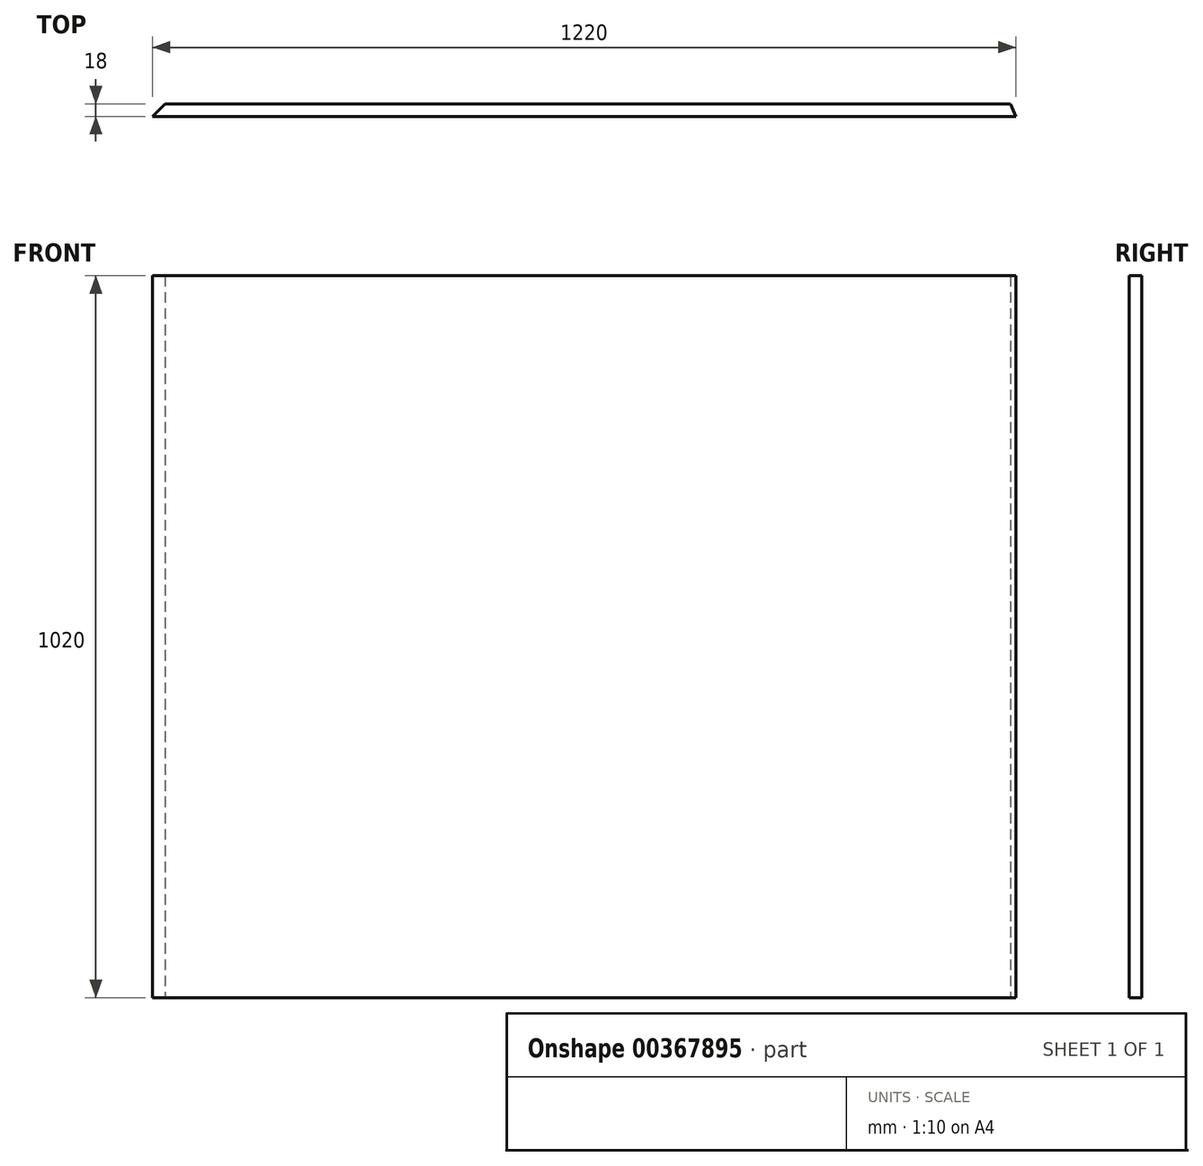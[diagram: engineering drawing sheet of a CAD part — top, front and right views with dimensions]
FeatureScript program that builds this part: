
annotation { "Feature Type Name" : "Feature", "Feature Type Description" : "" }
export const myFeature = defineFeature(function(context is Context, id is Id, definition is map)
    precondition{}
    {
        {
            var Q0;
            Q0=qCreatedBy(makeId("Top.planeOp"),FACE);
            var sketch = newSketch(context, id + "F0", { "sketchPlane" : qUnion([Q0])});
            skLineSegment(sketch, "E0", {"start": v(0, 0) * mm, "end": v(-1220, 0) * mm});
            skLineSegment(sketch, "E1", {"start": v(-1220, 0) * mm, "end": v(-1202, 18) * mm});
            skLineSegment(sketch, "E2", {"start": v(-1202, 18) * mm, "end": v(-7.46, 18) * mm});
            skLineSegment(sketch, "E3", {"start": v(-7.46, 18) * mm, "end": v(0, 0) * mm});
            skSolve(sketch);
        }
        {
            var Q0;
            Q0 = qSketchRegion(id + "F0", true);
            extrude(context, id + "F1", {"entities" : qUnion([Q0]), "depth" : 1020 * mm});
        }
    });
